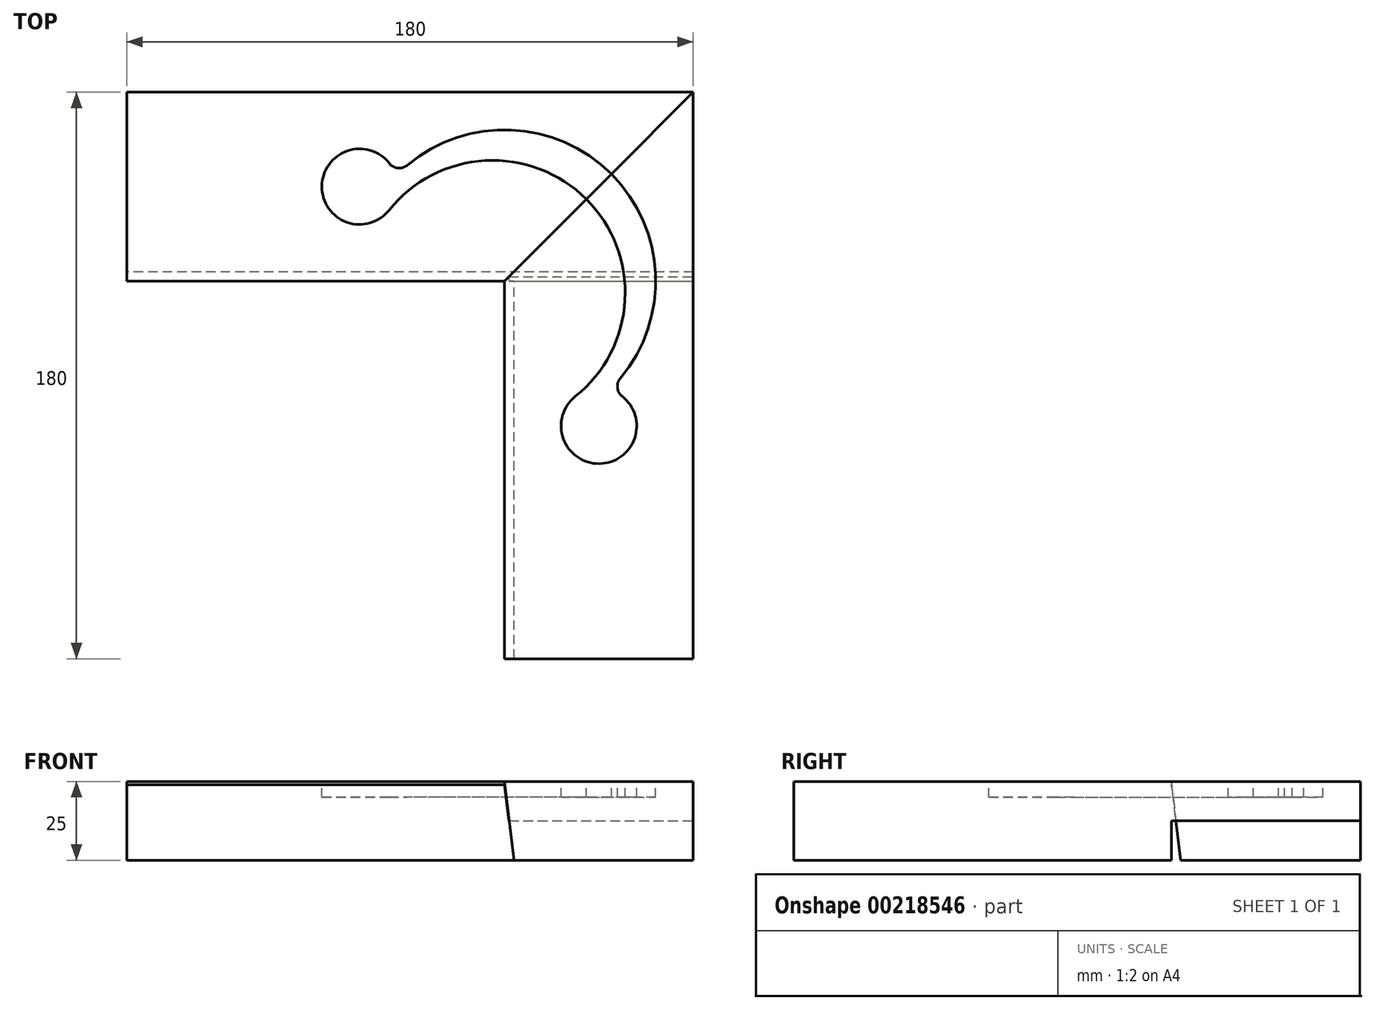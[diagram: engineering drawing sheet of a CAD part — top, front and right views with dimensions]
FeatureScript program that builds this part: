
annotation { "Feature Type Name" : "Feature", "Feature Type Description" : "" }
export const myFeature = defineFeature(function(context is Context, id is Id, definition is map)
    precondition{}
    {
        {
            assignVariable(context, id + "F0", {"name" : "thickness", "anyValue" : 25 * mm});
        }
        {
            var Q0;
            Q0=qCreatedBy(makeId("Top.planeOp"),FACE);
            var sketch = newSketch(context, id + "F1", { "sketchPlane" : qUnion([Q0])});
            skLineSegment(sketch, "E0.bottom", {"start": v(0, 0) * mm, "end": v(-120, 0) * mm});
            skLineSegment(sketch, "E0.top", {"start": v(60, 60) * mm, "end": v(-120, 60) * mm});
            skLineSegment(sketch, "E0.right", {"start": v(-120, 0) * mm, "end": v(-120, 60) * mm});
            skLineSegment(sketch, "E1", {"start": v(0, 0) * mm, "end": v(12.68, 12.68) * mm});
            skLineSegment(sketch, "E2.trimOffspring", {"start": v(47.32, 47.32) * mm, "end": v(60, 60) * mm});
            skLineSegment(sketch, "E3", {"start": v(12.68, 12.68) * mm, "end": v(47.32, 47.32) * mm});
            skSolve(sketch);
        }
        {
            var Q0;
            Q0=makeQuery(id+"F1.imprint","IMPRINT",FACE,{"disambiguationData":[TD([[makeQuery(id+"F1.imprint","IMPRINT",EDGE,{"derivedFrom":sQuery(id+"F1.wireOp",EDGE,"E0.bottom")}),-1.0]])]});
            extrude(context, id + "F2", {"entities" : qUnion([Q0]), "depth" : getVariable(context, 'thickness') / 2});
        }
        {
            var Q0;
            Q0=qCreatedBy(makeId("Top.planeOp"),FACE);
            var sketch = newSketch(context, id + "F3", { "sketchPlane" : qUnion([Q0])});
            skLineSegment(sketch, "E4.bottom", {"start": v(60, 0) * mm, "end": v(-120, 0) * mm});
            skLineSegment(sketch, "E4.top", {"start": v(60, 60) * mm, "end": v(-120, 60) * mm});
            skLineSegment(sketch, "E4.left", {"start": v(60, 0) * mm, "end": v(60, 60) * mm});
            skLineSegment(sketch, "E4.right", {"start": v(-120, 0) * mm, "end": v(-120, 60) * mm});
            skSolve(sketch);
        }
        {
            var Q0;
            Q0=qSketchRegion(id+"F3",true);
            extrude(context, id + "F4", {"entities" : qUnion([Q0]), "operationType" : NewBodyOperationType.ADD, "oppositeDirection" : true, "depth" : getVariable(context, 'thickness') / 2});
        }
        {
            var Q0;
            Q0=makeQuery(id+"F4.opExtrude","CAP_EDGE",EDGE,{"disambiguationData":[OSD([sQuery(id+"F3.wireOp",EDGE,"E4.bottom")])],"isStart":false});
            chamfer(context, id + "F5", {"entities" : qUnion([Q0]), "chamferType" : ChamferType.OFFSET_ANGLE, "width" : 24 * mm, "oppositeDirection" : true, "angle" : 7 * degree, "tangentPropagation" : true});
        }
        {
            var Q0;
            Q0=qCreatedBy(makeId("Top.planeOp"),FACE);
            var sketch = newSketch(context, id + "F6", { "sketchPlane" : qUnion([Q0])});
            skLineSegment(sketch, "E5.bottom", {"start": v(0, 60) * mm, "end": v(60, 60) * mm});
            skLineSegment(sketch, "E5.top", {"start": v(0, -120) * mm, "end": v(60, -120) * mm});
            skLineSegment(sketch, "E5.left", {"start": v(0, 60) * mm, "end": v(0, -120) * mm});
            skLineSegment(sketch, "E5.right", {"start": v(60, 60) * mm, "end": v(60, -120) * mm});
            skLineSegment(sketch, "E6", {"start": v(0, 0) * mm, "end": v(12.68, 12.68) * mm});
            skLineSegment(sketch, "E7.trimOffspring", {"start": v(47.32, 47.32) * mm, "end": v(60, 60) * mm});
            skLineSegment(sketch, "E8", {"start": v(12.68, 12.68) * mm, "end": v(47.32, 47.32) * mm});
            skSolve(sketch);
        }
        {
            var Q0;
            {var subQ0=sQuery(id+"F6.wireOp",EDGE,"E5.top");Q0=makeQuery(id+"F6.imprint","IMPRINT",FACE,{"disambiguationData":[TD([[makeQuery(id+"F6.imprint","IMPRINT",EDGE,{"derivedFrom":subQ0}),1.0]])]});}
            extrude(context, id + "F7", {"entities" : qUnion([Q0]), "depth" : getVariable(context, 'thickness') / 2});
        }
        {
            var Q0;
            Q0=makeQuery(id+"F7.opExtrude","CAP_FACE",FACE,{"disambiguationData":[OSD([sQuery(id+"F6.wireOp",EDGE,"E5.top"),sQuery(id+"F6.wireOp",EDGE,"E5.left"),sQuery(id+"F6.wireOp",EDGE,"E5.right"),sQuery(id+"F6.wireOp",EDGE,"E6"),sQuery(id+"F6.wireOp",EDGE,"vZ8xgZ4W-Jopo-DPU0-gVDj-uFKTXcaNRzzS"),sQuery(id+"F6.wireOp",EDGE,"E7.trimOffspring"),sQuery(id+"F6.wireOp",EDGE,"2ba47d57-804e-419a-9e10-b9584deecd73.filletArc"),sQuery(id+"F6.wireOp",EDGE,"09b8c270-4e6c-4ded-aa57-54961d685d8d.filletArc")])],"isStart":true});
            var sketch = newSketch(context, id + "F8", { "sketchPlane" : qUnion([Q0])});
            skLineSegment(sketch, "E9.bottom", {"start": v(0, 120) * mm, "end": v(60, 120) * mm});
            skLineSegment(sketch, "E9.top", {"start": v(0, 0) * mm, "end": v(60, 0) * mm});
            skLineSegment(sketch, "E9.left", {"start": v(0, 120) * mm, "end": v(0, 0) * mm});
            skLineSegment(sketch, "E9.right", {"start": v(60, 120) * mm, "end": v(60, 0) * mm});
            skSolve(sketch);
        }
        {
            var Q0;
            Q0=makeQuery(id+"F8.imprint","IMPRINT",FACE,{"disambiguationData":[TD([[makeQuery(id+"F8.imprint","IMPRINT",EDGE,{"derivedFrom":sQuery(id+"F8.wireOp",EDGE,"E9.bottom")}),-1.0]])]});
            extrude(context, id + "F9", {"entities" : qUnion([Q0]), "operationType" : NewBodyOperationType.ADD, "depth" : getVariable(context, 'thickness') / 2});
        }
        {
            var Q0;
            Q0=makeQuery(id+"F9.opExtrude","CAP_EDGE",EDGE,{"disambiguationData":[OSD([sQuery(id+"F8.wireOp",EDGE,"E9.left")])],"isStart":false});
            chamfer(context, id + "F10", {"entities" : qUnion([Q0]), "chamferType" : ChamferType.OFFSET_ANGLE, "width" : getVariable(context, 'thickness'), "oppositeDirection" : false, "angle" : 7 * degree, "tangentPropagation" : true});
        }
        {
            var Q0;
            Q0=makeQuery(id+"F2.opExtrude","CAP_FACE",FACE,{"disambiguationData":[OSD([sQuery(id+"F1.wireOp",EDGE,"E0.bottom"),sQuery(id+"F1.wireOp",EDGE,"E0.top"),sQuery(id+"F1.wireOp",EDGE,"E0.right"),sQuery(id+"F1.wireOp",EDGE,"E1"),sQuery(id+"F1.wireOp",EDGE,"E2.trimOffspring"),sQuery(id+"F1.wireOp",EDGE,"E3")])],"isStart":false});
            var Q1;
            Q1=makeQuery(id+"F2.opExtrude","CAP_VERTEX",VERTEX,{"disambiguationData":[OSD([sQuery(id+"F1.wireOp",EDGE,"E0.top"),sQuery(id+"F1.wireOp",EDGE,"E2.trimOffspring")])],"isStart":false});
            cPlane(context, id + "F11", {"entities" : qUnion([Q0, Q1]), "cplaneType" : CPlaneType.PLANE_POINT, "offset" : 25 * mm, "width" : 150 * mm, "height" : 150 * mm});
        }
        {
            var Q0;
            Q0=qCreatedBy(id+"F11.planeOp",FACE);
            var sketch = newSketch(context, id + "F12", { "sketchPlane" : qUnion([Q0])});
            skArc(sketch, "E10", {"start": v(36.82, -30.88) * mm, "mid": v(33.98, 33.98) * mm, "end": v(-30.88, 36.82) * mm});
            skArc(sketch, "E11", {"start": v(22.51, -36.66) * mm, "mid": v(30.05, -58.04) * mm, "end": v(37.41, -36.6) * mm});
            skArc(sketch, "E12", {"start": v(22.51, -36.66) * mm, "mid": v(26.02, 26.02) * mm, "end": v(-36.66, 22.51) * mm});
            skLineSegment(sketch, "E13", {"start": v(-36.66, 22.51) * mm, "end": v(-36.66, 22.51) * mm});
            skArc(sketch, "E14", {"start": v(36.82, -30.88) * mm, "mid": v(35.9, -33.87) * mm, "end": v(37.41, -36.6) * mm});
            skLineSegment(sketch, "E15", {"start": v(30, 30) * mm, "end": v(33.98, 33.98) * mm, "construction": true});
            skLineSegment(sketch, "E16", {"start": v(30, 30) * mm, "end": v(26.02, 26.02) * mm, "construction": true});
            skLineSegment(sketch, "E17", {"start": v(0, 0) * mm, "end": v(-19.43, -19.43) * mm, "construction": true});
            skLineSegment(sketch, "E18", {"start": v(-46.04, 60) * mm, "end": v(-46.04, 0) * mm, "construction": true});
            skArc(sketch, "E19", {"start": v(-36.6, 37.41) * mm, "mid": v(-33.87, 35.9) * mm, "end": v(-30.88, 36.82) * mm});
            skArc(sketch, "E20", {"start": v(-36.6, 37.41) * mm, "mid": v(-58.04, 30.05) * mm, "end": v(-36.66, 22.51) * mm});
            skLineSegment(sketch, "E21.MirrorCS", {"start": v(60, -46.04) * mm, "end": v(0, -46.04) * mm, "construction": true});
            skSolve(sketch);
        }
        {
            var Q0;
            Q0=qSketchRegion(id+"F12",true);
            extrude(context, id + "F13", {"entities" : qUnion([Q0]), "operationType" : NewBodyOperationType.REMOVE, "oppositeDirection" : true, "depth" : 5 * mm});
        }
    });
